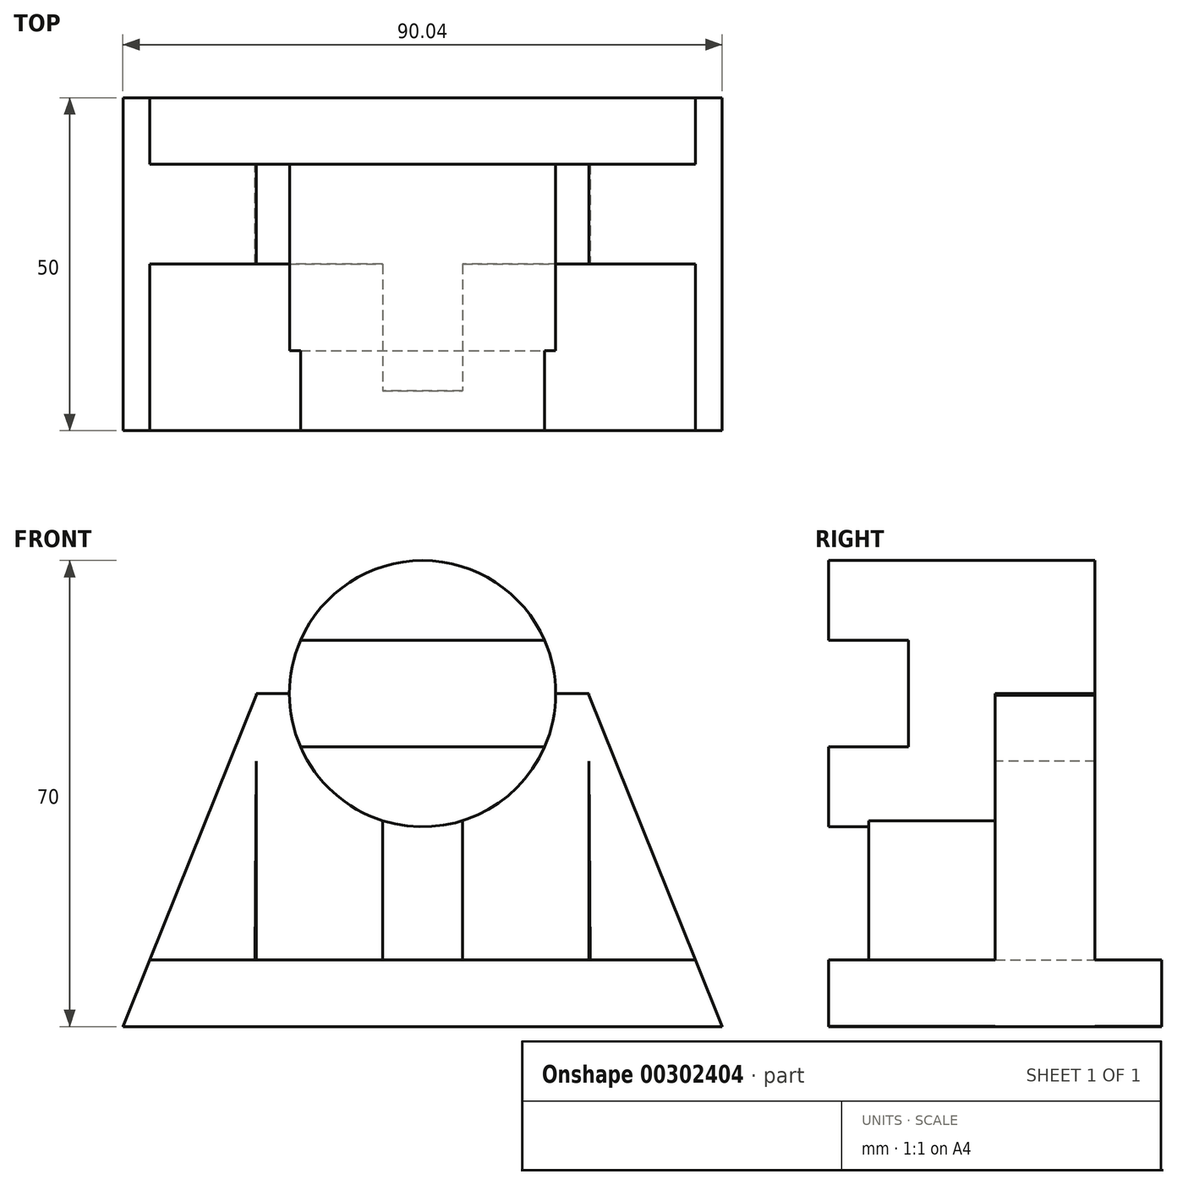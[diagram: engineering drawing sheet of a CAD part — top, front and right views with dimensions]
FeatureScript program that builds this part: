
annotation { "Feature Type Name" : "Feature", "Feature Type Description" : "" }
export const myFeature = defineFeature(function(context is Context, id is Id, definition is map)
    precondition{}
    {
        {
            var Q0;
            Q0=qCreatedBy(makeId("Top.planeOp"),FACE);
            var sketch = newSketch(context, id + "F0", { "sketchPlane" : qUnion([Q0])});
            skLineSegment(sketch, "E0.bottom", {"start": v(-45, -25) * mm, "end": v(45, -25) * mm});
            skLineSegment(sketch, "E0.top", {"start": v(-45, 25) * mm, "end": v(45, 25) * mm});
            skLineSegment(sketch, "E0.left", {"start": v(-45, -25) * mm, "end": v(-45, 25) * mm});
            skLineSegment(sketch, "E0.right", {"start": v(45, -25) * mm, "end": v(45, 25) * mm});
            skPoint(sketch, "E0.middle", {"position": v(0, 0) * mm});
            skSolve(sketch);
        }
        {
            var Q0;
            Q0=makeQuery(id+"F0.imprint","IMPRINT",FACE,{"disambiguationData":[TD([[makeQuery(id+"F0.imprint","IMPRINT",EDGE,{"derivedFrom":sQuery(id+"F0.wireOp",EDGE,"E0.bottom")}),1.0]])]});
            extrude(context, id + "F1", {"entities" : qUnion([Q0]), "depth" : 10 * mm});
        }
        {
            var Q0;
            Q0=makeQuery(id+"F1.opExtrude","SWEPT_FACE",FACE,{"disambiguationData":[OSD([sQuery(id+"F0.wireOp",EDGE,"E0.bottom")])]});
            var sketch = newSketch(context, id + "F2", { "sketchPlane" : qUnion([Q0])});
            skCircle(sketch, "E1", {"center": v(0, 50) * mm, "radius": 20 * mm});
            skSolve(sketch);
        }
        {
            var Q0;
            Q0=makeQuery(id+"F2.imprint","IMPRINT",FACE,{"disambiguationData":[TD([[makeQuery(id+"F2.imprint","IMPRINT",EDGE,{"derivedFrom":sQuery(id+"F2.wireOp",EDGE,"E1")}),1.0]])]});
            var Q1;
            Q1=sQuery(id+"F2.wireOp",EDGE,"E1");
            extrude(context, id + "F3", {"entities" : qUnion([Q0]), "surfaceEntities" : qUnion([Q1]), "oppositeDirection" : true, "depth" : 40 * mm});
        }
        {
            var Q0;
            Q0=makeQuery(id+"F3.opExtrude","CAP_FACE",FACE,{"disambiguationData":[OSD([sQuery(id+"F2.wireOp",EDGE,"E1")])],"isStart":true});
            var sketch = newSketch(context, id + "F4", { "sketchPlane" : qUnion([Q0])});
            skLineSegment(sketch, "E2.bottom", {"start": v(-38.4, 42) * mm, "end": v(38.4, 42) * mm});
            skLineSegment(sketch, "E2.top", {"start": v(-38.4, 58) * mm, "end": v(38.4, 58) * mm});
            skLineSegment(sketch, "E2.left", {"start": v(-38.4, 42) * mm, "end": v(-38.4, 58) * mm});
            skLineSegment(sketch, "E2.right", {"start": v(38.4, 42) * mm, "end": v(38.4, 58) * mm});
            skPoint(sketch, "E2.middle", {"position": v(0, 50) * mm});
            skSolve(sketch);
        }
        {
            var Q0;
            {var subQ0=sQuery(id+"F4.wireOp",EDGE,"E2.right");Q0=makeQuery(id+"F4.imprint","IMPRINT",FACE,{"disambiguationData":[TD([[makeQuery(id+"F4.imprint","IMPRINT",EDGE,{"derivedFrom":subQ0}),1.0]])]});}
            var Q1;
            {var subQ0=sQuery(id+"F4.wireOp",EDGE,"E2.left");Q1=makeQuery(id+"F4.imprint","IMPRINT",FACE,{"disambiguationData":[TD([[makeQuery(id+"F4.imprint","IMPRINT",EDGE,{"derivedFrom":subQ0}),-1.0]])]});}
            var Q2;
            {var subQ0=sQuery(id+"F4.wireOp",EDGE,"E2.bottom");var subQ1=makeQuery(id+"F3.opExtrude","CAP_EDGE",EDGE,{"disambiguationData":[OSD([sQuery(id+"F2.wireOp",EDGE,"E1")])],"isStart":true});var subQ2=makeQuery(id+"F4.imprint","INTERSECT",VERTEX,{"disambiguationData":[OD(0.0)],"derivedFrom":[subQ1,subQ0]});Q2=makeQuery(id+"F4.imprint","IMPRINT",FACE,{"disambiguationData":[TD([[makeQuery(id+"F4.imprint","IMPRINT",EDGE,{"disambiguationData":[TD([[subQ2,-1.0]])],"derivedFrom":subQ0}),1.0]])]});}
            extrude(context, id + "F5", {"entities" : qUnion([Q0, Q1, Q2]), "operationType" : NewBodyOperationType.REMOVE, "oppositeDirection" : true, "depth" : 12 * mm});
        }
        {
            var Q0;
            Q0=makeQuery(id+"F1.opExtrude","CAP_FACE",FACE,{"disambiguationData":[OSD([sQuery(id+"F0.wireOp",EDGE,"E0.bottom"),sQuery(id+"F0.wireOp",EDGE,"E0.top"),sQuery(id+"F0.wireOp",EDGE,"E0.left"),sQuery(id+"F0.wireOp",EDGE,"E0.right")])],"isStart":false});
            var sketch = newSketch(context, id + "F6", { "sketchPlane" : qUnion([Q0])});
            skLineSegment(sketch, "E3.bottom", {"start": v(6, 0) * mm, "end": v(-6, 0) * mm});
            skLineSegment(sketch, "E3.top", {"start": v(6, -19) * mm, "end": v(-6, -19) * mm});
            skLineSegment(sketch, "E3.left", {"start": v(6, 0) * mm, "end": v(6, -19) * mm});
            skLineSegment(sketch, "E3.right", {"start": v(-6, 0) * mm, "end": v(-6, -19) * mm});
            skPoint(sketch, "E3.middle", {"position": v(0, -9.5) * mm});
            skSolve(sketch);
        }
        {
            var Q0;
            Q0=makeQuery(id+"F6.imprint","IMPRINT",FACE,{"disambiguationData":[TD([[makeQuery(id+"F6.imprint","IMPRINT",EDGE,{"derivedFrom":sQuery(id+"F6.wireOp",EDGE,"E3.bottom")}),1.0]])]});
            extrude(context, id + "F7", {"entities" : qUnion([Q0]), "operationType" : NewBodyOperationType.ADD, "depth" : 25 * mm});
        }
        {
            var Q0;
            Q0=makeQuery(id+"F1.opExtrude","CAP_FACE",FACE,{"disambiguationData":[OSD([sQuery(id+"F0.wireOp",EDGE,"E0.bottom"),sQuery(id+"F0.wireOp",EDGE,"E0.top"),sQuery(id+"F0.wireOp",EDGE,"E0.left"),sQuery(id+"F0.wireOp",EDGE,"E0.right")])],"isStart":false});
            var sketch = newSketch(context, id + "F8", { "sketchPlane" : qUnion([Q0])});
            skLineSegment(sketch, "E4.bottom", {"start": v(25, 0) * mm, "end": v(-25, 0) * mm});
            skLineSegment(sketch, "E4.top", {"start": v(25, 15) * mm, "end": v(-25, 15) * mm});
            skLineSegment(sketch, "E4.left", {"start": v(25, 0) * mm, "end": v(25, 15) * mm});
            skLineSegment(sketch, "E4.right", {"start": v(-25, 0) * mm, "end": v(-25, 15) * mm});
            skPoint(sketch, "E4.middle", {"position": v(0, 7.5) * mm});
            skSolve(sketch);
        }
        {
            var Q0;
            Q0=makeQuery(id+"F8.imprint","IMPRINT",FACE,{"disambiguationData":[TD([[makeQuery(id+"F8.imprint","IMPRINT",EDGE,{"derivedFrom":sQuery(id+"F8.wireOp",EDGE,"E4.top")}),1.0]])]});
            extrude(context, id + "F9", {"entities" : qUnion([Q0]), "depth" : 40 * mm});
        }
        {
            var Q0;
            Q0=qCreatedBy(makeId("Front.planeOp"),FACE);
            var sketch = newSketch(context, id + "F10", { "sketchPlane" : qUnion([Q0])});
            skLineSegment(sketch, "E5", {"start": v(-24.95, 49.93) * mm, "end": v(-45.02, 0) * mm});
            skLineSegment(sketch, "E6", {"start": v(-45.02, 0) * mm, "end": v(-25.22, 0) * mm});
            skLineSegment(sketch, "E7", {"start": v(-25.22, 0) * mm, "end": v(-24.95, 49.93) * mm});
            skSolve(sketch);
        }
        {
            var Q0;
            Q0=makeQuery(id+"F10.imprint","IMPRINT",FACE,{"disambiguationData":[TD([[makeQuery(id+"F10.imprint","IMPRINT",EDGE,{"derivedFrom":sQuery(id+"F10.wireOp",EDGE,"E5")}),1.0]])]});
            extrude(context, id + "F11", {"entities" : qUnion([Q0]), "oppositeDirection" : true, "depth" : 15 * mm});
        }
        {
            var Q0;
            Q0=makeQuery(id+"F11.opExtrude","SWEPT_BODY",BODY,{"disambiguationData":[OSD([sQuery(id+"F10.wireOp",EDGE,"E5"),sQuery(id+"F10.wireOp",EDGE,"E6"),sQuery(id+"F10.wireOp",EDGE,"E7")])]});
            var Q1;
            Q1=makeQuery(id+"F11.opExtrude","SWEPT_FACE",FACE,{"disambiguationData":[OSD([sQuery(id+"F10.wireOp",EDGE,"E5")])]});
            var Q2;
            Q2=makeQuery(id+"F11.opExtrude","CAP_FACE",FACE,{"disambiguationData":[OSD([sQuery(id+"F10.wireOp",EDGE,"E5"),sQuery(id+"F10.wireOp",EDGE,"E6"),sQuery(id+"F10.wireOp",EDGE,"E7")])],"isStart":true});
            var Q3;
            Q3=qCreatedBy(makeId("Right.planeOp"),FACE);
            mirror(context, id + "F12", {"operationType" : NewBodyOperationType.ADD, "entities" : qUnion([Q0]), "faces" : qUnion([Q1, Q2]), "mirrorPlane" : qUnion([Q3])});
        }
        {
            var Q0;
            {var subQ2=sQuery(id+"F10.wireOp",EDGE,"E5");Q0=makeQuery(id+"F12.boolean.opBoolean","SPLIT",FACE,{"disambiguationData":[TD([makeQuery(id+"F9.opExtrude","SWEPT_FACE",FACE,{"disambiguationData":[OSD([sQuery(id+"F8.wireOp",EDGE,"E4.right")])]})])],"derivedFrom":makeQuery(id+"F11.opExtrude","SWEPT_FACE",FACE,{"disambiguationData":[OSD([subQ2])]})});}
            var sketch = newSketch(context, id + "F13", { "sketchPlane" : qUnion([Q0])});
            skLineSegment(sketch, "E8.bottom", {"start": v(34, 7.4) * mm, "end": v(-49, 7.4) * mm});
            skLineSegment(sketch, "E8.top", {"start": v(34, -19.42) * mm, "end": v(-49, -19.42) * mm});
            skLineSegment(sketch, "E8.left", {"start": v(34, 7.4) * mm, "end": v(34, -19.42) * mm});
            skLineSegment(sketch, "E8.right", {"start": v(-49, 7.4) * mm, "end": v(-49, -19.42) * mm});
            skPoint(sketch, "E8.middle", {"position": v(-7.5, -6.01) * mm});
            skSolve(sketch);
        }
        {
            var Q0;
            Q0=makeQuery(id+"F13.imprint","IMPRINT",FACE,{"disambiguationData":[TD([[makeQuery(id+"F13.imprint","IMPRINT",EDGE,{"derivedFrom":sQuery(id+"F13.wireOp",EDGE,"E8.top")}),-1.0]])]});
            extrude(context, id + "F14", {"entities" : qUnion([Q0]), "operationType" : NewBodyOperationType.REMOVE, "depth" : 10 * mm});
        }
        {
            var Q0;
            {var subQ2=sQuery(id+"F10.wireOp",EDGE,"E5");Q0=makeQuery(id+"F12.boolean.opBoolean","SPLIT",FACE,{"disambiguationData":[TD([makeQuery(id+"F9.opExtrude","SWEPT_FACE",FACE,{"disambiguationData":[OSD([sQuery(id+"F8.wireOp",EDGE,"E4.left")])]})])],"derivedFrom":makeQuery(id+"F12.opPattern","COPY",FACE,{"derivedFrom":makeQuery(id+"F11.opExtrude","SWEPT_FACE",FACE,{"disambiguationData":[OSD([subQ2])]}),"instanceName":"1"})});}
            var sketch = newSketch(context, id + "F15", { "sketchPlane" : qUnion([Q0])});
            skLineSegment(sketch, "E9.bottom", {"start": v(-31.8, 9.33) * mm, "end": v(46.8, 9.33) * mm});
            skLineSegment(sketch, "E9.top", {"start": v(-31.8, -21.36) * mm, "end": v(46.8, -21.36) * mm});
            skLineSegment(sketch, "E9.left", {"start": v(-31.8, 9.33) * mm, "end": v(-31.8, -21.36) * mm});
            skLineSegment(sketch, "E9.right", {"start": v(46.8, 9.33) * mm, "end": v(46.8, -21.36) * mm});
            skPoint(sketch, "E9.middle", {"position": v(7.5, -6.01) * mm});
            skSolve(sketch);
        }
        {
            var Q0;
            Q0=makeQuery(id+"F15.imprint","IMPRINT",FACE,{"disambiguationData":[TD([[makeQuery(id+"F15.imprint","IMPRINT",EDGE,{"derivedFrom":sQuery(id+"F15.wireOp",EDGE,"E9.top")}),1.0]])]});
            extrude(context, id + "F16", {"entities" : qUnion([Q0]), "operationType" : NewBodyOperationType.REMOVE, "depth" : 25 * mm});
        }
    });
